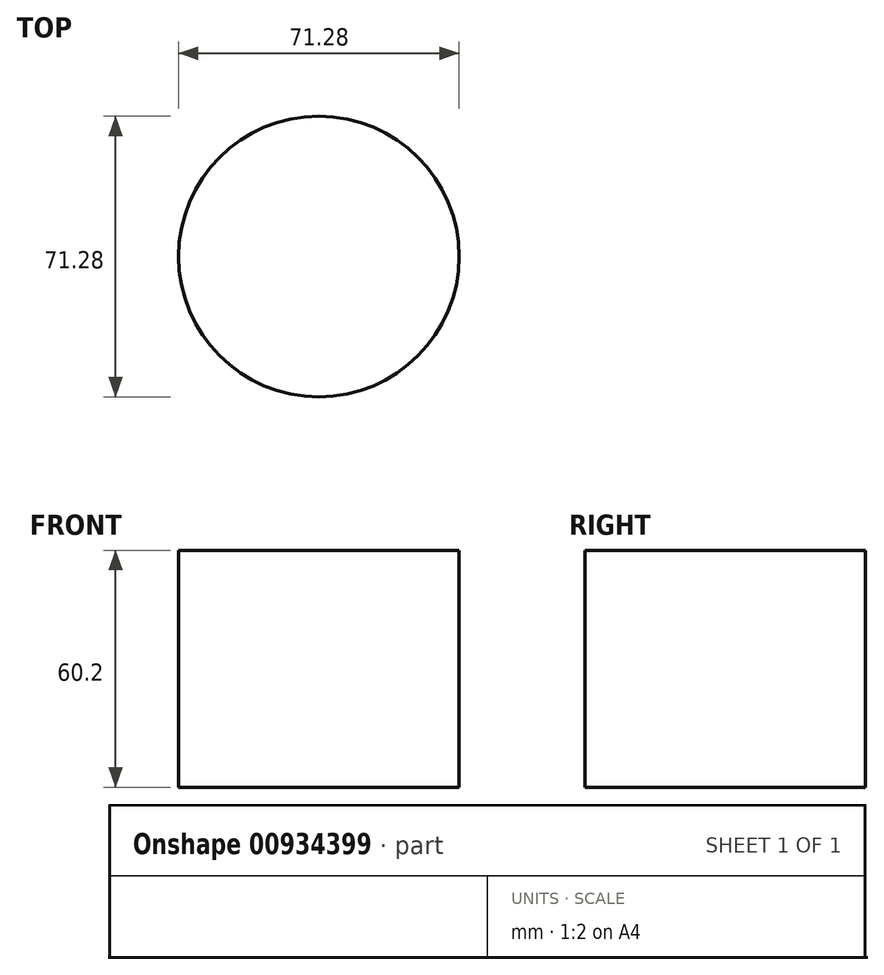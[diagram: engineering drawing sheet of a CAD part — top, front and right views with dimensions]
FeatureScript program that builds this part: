
annotation { "Feature Type Name" : "Feature", "Feature Type Description" : "" }
export const myFeature = defineFeature(function(context is Context, id is Id, definition is map)
    precondition{}
    {
        {
            var Q0;
            Q0=qCreatedBy(makeId("Top.planeOp"),FACE);
            var sketch = newSketch(context, id + "F0", { "sketchPlane" : qUnion([Q0])});
            skCircle(sketch, "E0", {"center": v(0, 0) * mm, "radius": 35.64 * mm});
            skSolve(sketch);
        }
        {
            var Q0;
            Q0 = qSketchRegion(id + "F0", true);
            extrude(context, id + "F1", {"entities" : qUnion([Q0]), "depth" : 60.2 * mm, "offsetDistance" : 25.4 * mm});
        }
    });
